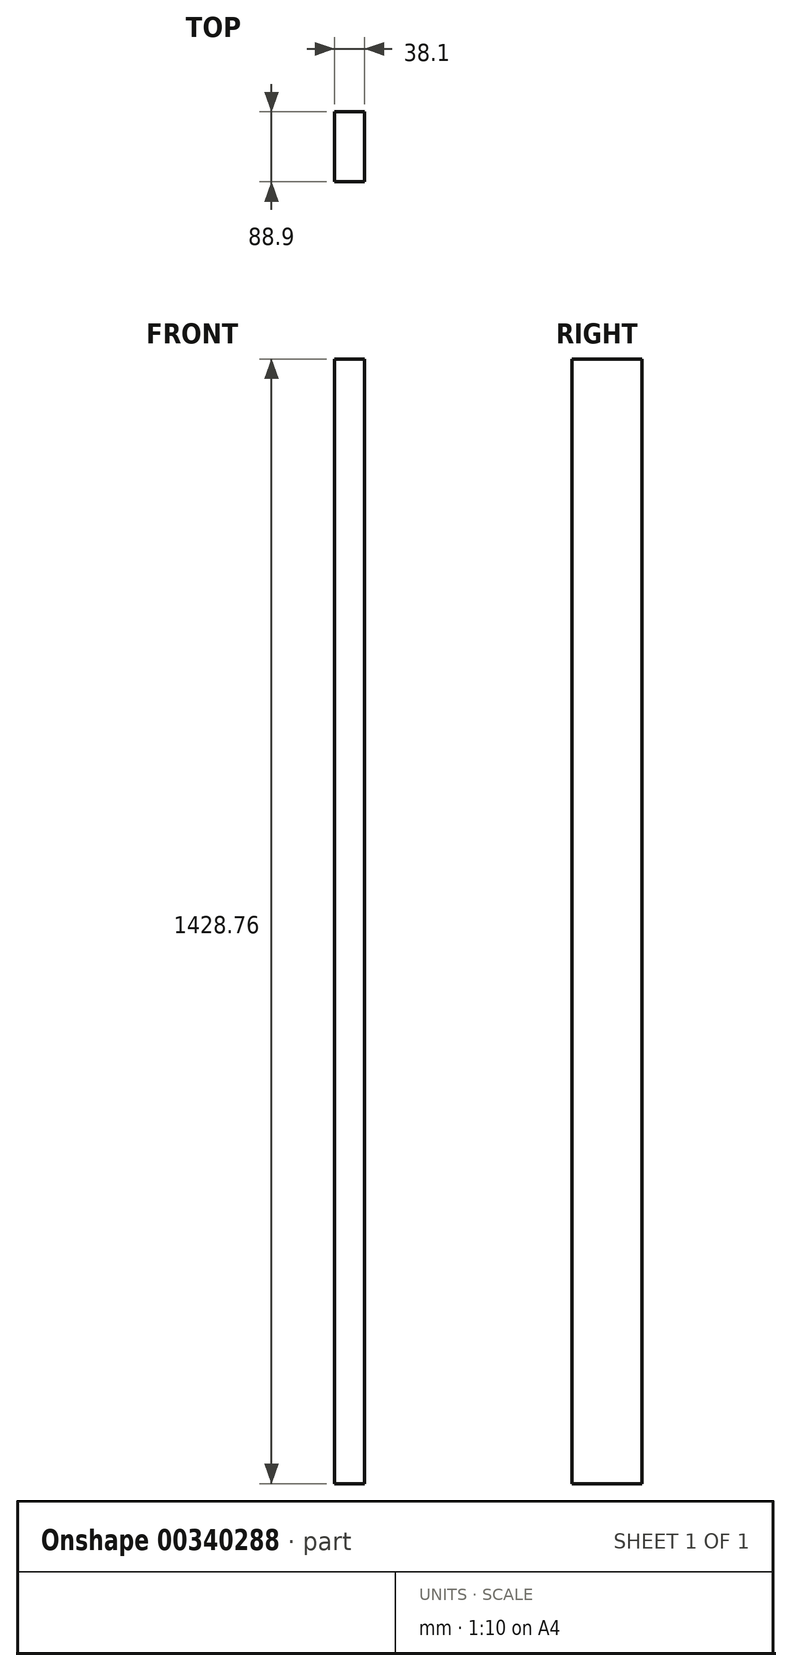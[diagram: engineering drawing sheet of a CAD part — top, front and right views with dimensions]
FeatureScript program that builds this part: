
annotation { "Feature Type Name" : "Feature", "Feature Type Description" : "" }
export const myFeature = defineFeature(function(context is Context, id is Id, definition is map)
    precondition{}
    {
        {
            var Q0;
            Q0=qCreatedBy(makeId("Top.planeOp"),FACE);
            var sketch = newSketch(context, id + "F0", { "sketchPlane" : qUnion([Q0])});
            skLineSegment(sketch, "E0.bottom", {"start": v(19.05, -44.45) * mm, "end": v(-19.05, -44.45) * mm});
            skLineSegment(sketch, "E0.top", {"start": v(19.05, 44.45) * mm, "end": v(-19.05, 44.45) * mm});
            skLineSegment(sketch, "E0.left", {"start": v(19.05, -44.45) * mm, "end": v(19.05, 44.45) * mm});
            skLineSegment(sketch, "E0.right", {"start": v(-19.05, -44.45) * mm, "end": v(-19.05, 44.45) * mm});
            skPoint(sketch, "E0.middle", {"position": v(0, 0) * mm});
            skSolve(sketch);
        }
        {
            var Q0;
            Q0 = qSketchRegion(id + "F0", true);
            extrude(context, id + "F1", {"entities" : qUnion([Q0]), "endBound" : BoundingType.SYMMETRIC, "depth" : 1428.75 * mm});
        }
    });
